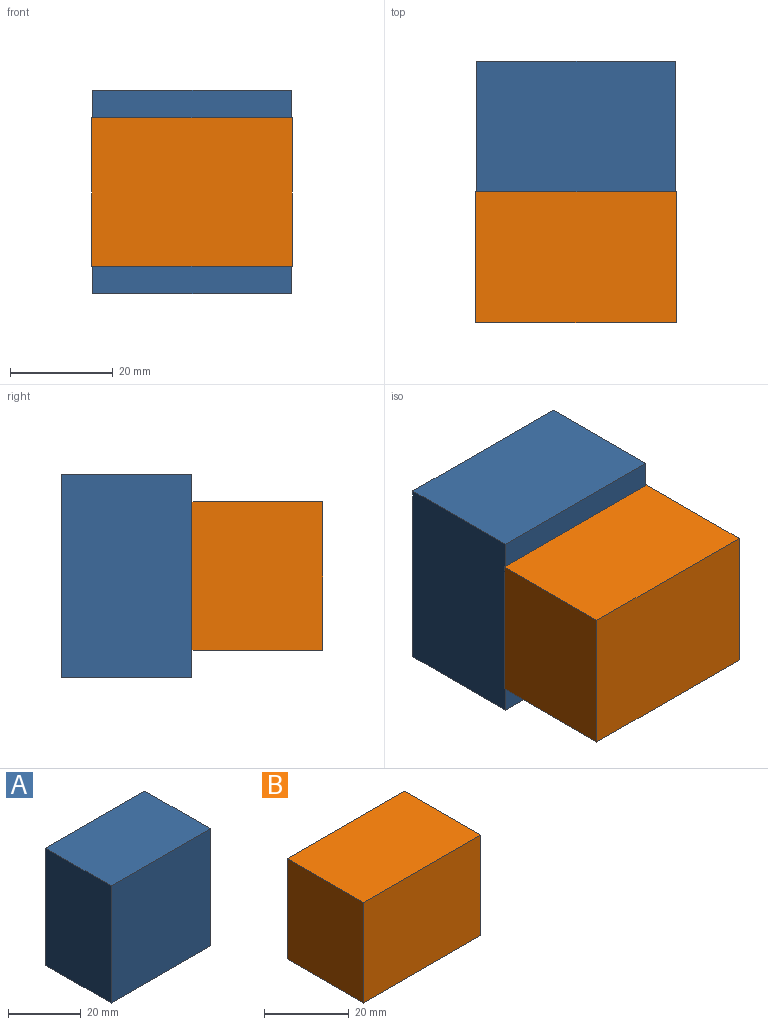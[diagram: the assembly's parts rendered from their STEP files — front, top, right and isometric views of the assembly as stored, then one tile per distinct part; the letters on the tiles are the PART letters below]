
ASSEMBLY  parts=2 mates=1
PART A: 6 faces, bbox 38.5x25.4x39.5 mm
  f0: plane 38.53x25.4mm, normal (0,0,-1), area 978.7mm2, adj f1,f3,f4,f5
  f1: plane 39.45x25.4mm, normal (1,0,0), area 1002.1mm2, adj f0,f2,f4,f5
  f2: plane 38.53x25.4mm, normal (0,0,1), area 978.7mm2, adj f1,f3,f4,f5
  f3: plane 39.45x25.4mm, normal (-1,0,0), area 1002.1mm2, adj f0,f2,f4,f5
  f4: plane 39.45x38.53mm, normal (0,-1,0), area 1520.1mm2, adj f0,f1,f2,f3
  f5: plane 39.45x38.53mm, normal (0,1,0), area 1520.1mm2, adj f0,f1,f2,f3
PART B: 6 faces, bbox 39x25.4x28.9 mm
  f0: plane 28.94x25.4mm, normal (-1,0,0), area 735.1mm2, adj f1,f3,f4,f5
  f1: plane 39.02x25.4mm, normal (0,0,-1), area 991.2mm2, adj f0,f2,f4,f5
  f2: plane 28.94x25.4mm, normal (1,0,0), area 735.1mm2, adj f1,f3,f4,f5
  f3: plane 39.02x25.4mm, normal (0,0,1), area 991.2mm2, adj f0,f2,f4,f5
  f4: plane 39.02x28.94mm, normal (0,-1,0), area 1129.3mm2, adj f0,f1,f2,f3
  f5: plane 39.02x28.94mm, normal (0,1,0), area 1129.3mm2, adj f0,f1,f2,f3
PLACE A rot(axis=(1,0,0),180deg) t=(1.12,-89.39,16)mm
PLACE B rot(axis=(1,0,0),180deg) t=(-123.66,-114.79,32.97)mm
MATE revolute B.f4 <-> A.f5  axis (0,1,0) through (-77.51,-89.39,-9.81)mm
